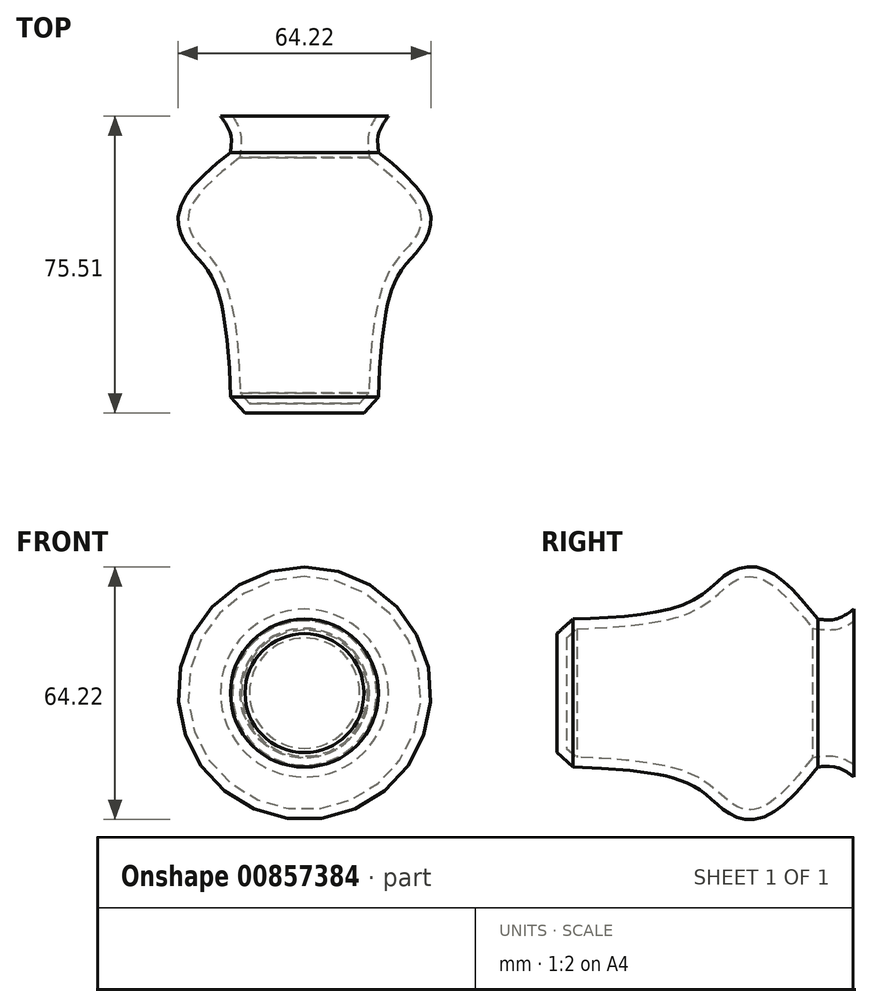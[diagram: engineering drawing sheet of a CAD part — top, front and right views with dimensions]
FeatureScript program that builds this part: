
annotation { "Feature Type Name" : "Feature", "Feature Type Description" : "" }
export const myFeature = defineFeature(function(context is Context, id is Id, definition is map)
    precondition{}
    {
        {
            var Q0;
            Q0=qCreatedBy(makeId("Top.planeOp"),FACE);
            var sketch = newSketch(context, id + "F0", { "sketchPlane" : qUnion([Q0])});
            skLineSegment(sketch, "E0", {"start": v(0, 0) * mm, "end": v(15.1, 0) * mm});
            skLineSegment(sketch, "E1", {"start": v(15.1, 0) * mm, "end": v(18.8, 4.1) * mm});
            skFitSpline(sketch, "E2", {"points": [v(18.8, 4.1) * mm, v(23.35, 34.2) * mm, v(30.52, 43.67) * mm, v(31.39, 52.86) * mm, v(18.8, 66.27) * mm], "startDerivative": vector(3.02, 101.72) * mm, "endDerivative": vector(-59.6, 47.2) * mm});
            skFitSpline(sketch, "E3", {"points": [v(18.8, 66.27) * mm, v(18.8, 70.96) * mm, v(21.34, 75.51) * mm], "startDerivative": vector(-1.2, 9.82) * mm, "endDerivative": vector(6.19, 8.68) * mm});
            skLineSegment(sketch, "E4", {"start": v(21.34, 75.51) * mm, "end": v(0, 75.51) * mm});
            skLineSegment(sketch, "E5", {"start": v(0, 75.51) * mm, "end": v(0, 75.51) * mm});
            skLineSegment(sketch, "E6", {"start": v(0, 75.51) * mm, "end": v(0, 0) * mm});
            skSolve(sketch);
        }
        {
            var Q0;
            Q0=makeQuery(id+"F0.imprint","IMPRINT",FACE,{"disambiguationData":[TD([[makeQuery(id+"F0.imprint","IMPRINT",EDGE,{"derivedFrom":sQuery(id+"F0.wireOp",EDGE,"E0")}),1.0]])]});
            var Q1;
            Q1=sQuery(id+"F0.wireOp",EDGE,"E6");
            revolve(context, id + "F1", {"surfaceOperationType" : NewSurfaceOperationType.NEW, "entities" : qUnion([Q0]), "axis" : qUnion([Q1]), "revolveType" : RevolveType.FULL});
        }
        {
            var Q0;
            Q0=makeQuery(id+"F1.opRevolve","SWEPT_FACE",FACE,{"disambiguationData":[OSD([sQuery(id+"F0.wireOp",EDGE,"E4")])]});
            shell(context, id + "F2", {"entities" : qUnion([Q0]), "thickness" : 2.5 * mm});
        }
    });
